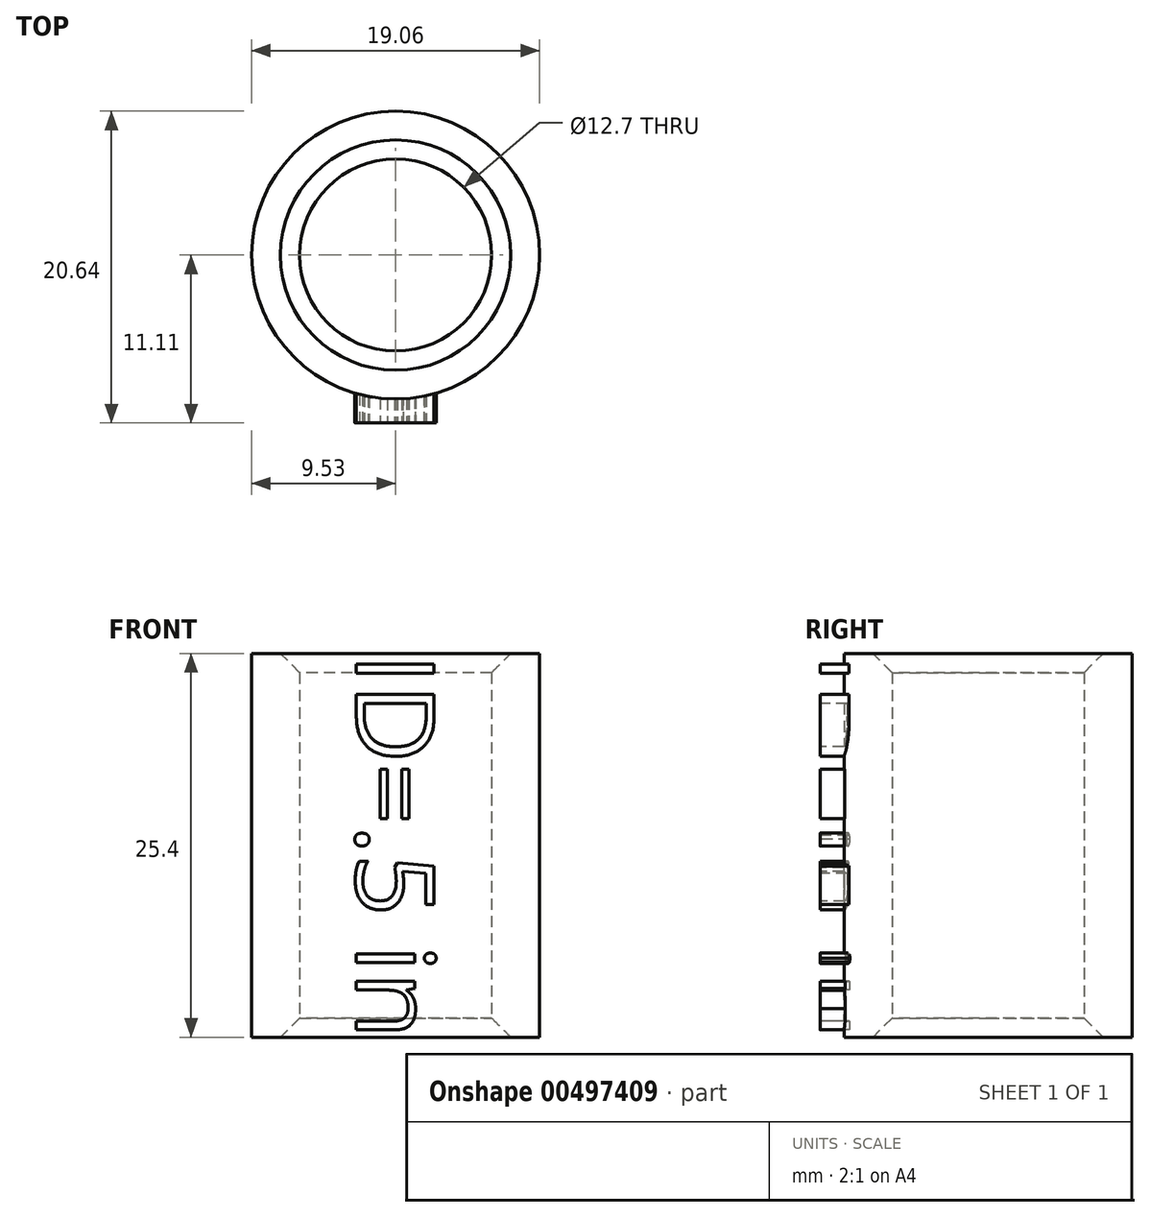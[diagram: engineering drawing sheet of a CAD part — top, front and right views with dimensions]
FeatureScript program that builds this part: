
annotation { "Feature Type Name" : "Feature", "Feature Type Description" : "" }
export const myFeature = defineFeature(function(context is Context, id is Id, definition is map)
    precondition{}
    {
        {
            var Q0;
            Q0=qCreatedBy(makeId("Top.planeOp"),FACE);
            var sketch = newSketch(context, id + "F0", { "sketchPlane" : qUnion([Q0])});
            skCircle(sketch, "E0", {"center": v(0, 0) * mm, "radius": 6.35 * mm});
            skCircle(sketch, "E1", {"center": v(0, 0) * mm, "radius": 9.53 * mm});
            skSolve(sketch);
        }
        {
            var Q0;
            Q0=makeQuery(id+"F0.imprint","IMPRINT",FACE,{"disambiguationData":[TD([[makeQuery(id+"F0.imprint","IMPRINT",EDGE,{"derivedFrom":sQuery(id+"F0.wireOp",EDGE,"E0")}),-1.0]])]});
            extrude(context, id + "F1", {"entities" : qUnion([Q0]), "depth" : 25.4 * mm});
        }
        {
            var Q0;
            Q0=qCreatedBy(makeId("Front.planeOp"),FACE);
            cPlane(context, id + "F2", {"entities" : qUnion([Q0]), "cplaneType" : CPlaneType.OFFSET, "offset" : 11.1 * mm, "width" : 152.4 * mm, "height" : 152.4 * mm});
        }
        {
            var Q0;
            Q0=qCreatedBy(id+"F2.planeOp",FACE);
            var sketch = newSketch(context, id + "F3", { "sketchPlane" : qUnion([Q0])});
            skText(sketch, "E2", { "text": "ID=.5 in", "fontName": "OpenSans-Regular.ttf"});
            const initialGuessF3  = {"E2": [-0.0026, 0.0254, 0, -1, 0.00518]};
            skSetInitialGuess(sketch, initialGuessF3);
            skSolve(sketch);
        }
        {
            var Q0;
            Q0 = qSketchRegion(id + "F3", true);
            extrude(context, id + "F4", {"entities" : qUnion([Q0]), "operationType" : NewBodyOperationType.ADD, "endBound" : BoundingType.UP_TO_NEXT, "oppositeDirection" : true, "depth" : 25.4 * mm});
        }
        {
            var Q0;
            Q0=makeQuery(id+"F1.opExtrude","CAP_EDGE",EDGE,{"disambiguationData":[OSD([sQuery(id+"F0.wireOp",EDGE,"E0")])],"isStart":false});
            var Q1;
            Q1=makeQuery(id+"F1.opExtrude","CAP_EDGE",EDGE,{"disambiguationData":[OSD([sQuery(id+"F0.wireOp",EDGE,"E0")])],"isStart":true});
            chamfer(context, id + "F5", {"entities" : qUnion([Q0, Q1]), "width" : 1.27 * mm, "tangentPropagation" : true});
        }
    });
